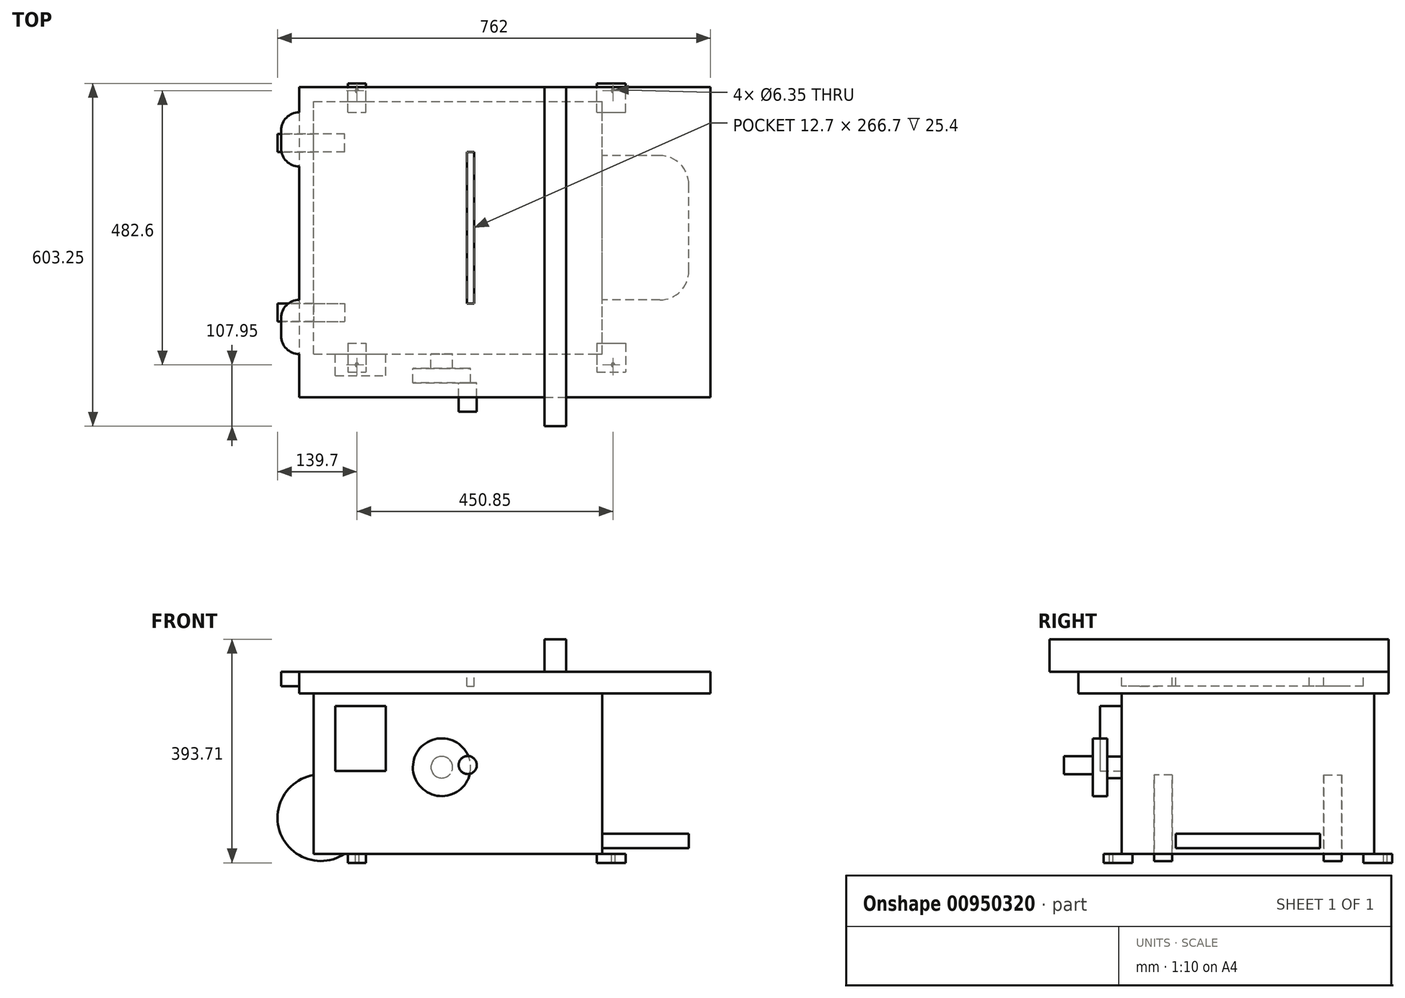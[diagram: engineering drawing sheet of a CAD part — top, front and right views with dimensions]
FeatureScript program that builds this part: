
annotation { "Feature Type Name" : "Feature", "Feature Type Description" : "" }
export const myFeature = defineFeature(function(context is Context, id is Id, definition is map)
    precondition{}
    {
        {
            var Q0;
            Q0=qCreatedBy(makeId("Top.planeOp"),FACE);
            var sketch = newSketch(context, id + "F0", { "sketchPlane" : qUnion([Q0])});
            skLineSegment(sketch, "E0.bottom", {"start": v(0, 0) * mm, "end": v(508, 0) * mm});
            skLineSegment(sketch, "E0.top", {"start": v(0, 444.5) * mm, "end": v(508, 444.5) * mm});
            skLineSegment(sketch, "E0.left", {"start": v(0, 0) * mm, "end": v(0, 444.5) * mm});
            skLineSegment(sketch, "E0.right", {"start": v(508, 0) * mm, "end": v(508, 444.5) * mm});
            skSolve(sketch);
        }
        {
            var Q0;
            Q0=qSketchRegion(id+"F0",true);
            extrude(context, id + "F1", {"entities" : qUnion([Q0]), "depth" : 282.57 * mm, "offsetDistance" : 25.4 * mm});
        }
        {
            var Q0;
            Q0=makeQuery(id+"F1.opExtrude","CAP_FACE",FACE,{"disambiguationData":[OSD([sQuery(id+"F0.wireOp",EDGE,"E0.bottom"),sQuery(id+"F0.wireOp",EDGE,"E0.top"),sQuery(id+"F0.wireOp",EDGE,"E0.left"),sQuery(id+"F0.wireOp",EDGE,"E0.right")])],"isStart":true});
            var sketch = newSketch(context, id + "F2", { "sketchPlane" : qUnion([Q0])});
            skLineSegment(sketch, "E1.bottom", {"start": v(60.32, -19.05) * mm, "end": v(92.07, -19.05) * mm});
            skLineSegment(sketch, "E1.top", {"start": v(60.32, 31.75) * mm, "end": v(92.07, 31.75) * mm});
            skLineSegment(sketch, "E1.left", {"start": v(60.32, -19.05) * mm, "end": v(60.32, 31.75) * mm});
            skLineSegment(sketch, "E1.right", {"start": v(92.07, -19.05) * mm, "end": v(92.07, 31.75) * mm});
            skLineSegment(sketch, "E2.bottom", {"start": v(498.48, -19.05) * mm, "end": v(549.28, -19.05) * mm});
            skLineSegment(sketch, "E2.top", {"start": v(498.48, 31.75) * mm, "end": v(549.28, 31.75) * mm});
            skLineSegment(sketch, "E2.left", {"start": v(498.48, -19.05) * mm, "end": v(498.48, 31.75) * mm});
            skLineSegment(sketch, "E2.right", {"start": v(549.28, -19.05) * mm, "end": v(549.28, 31.75) * mm});
            skLineSegment(sketch, "E3.bottom", {"start": v(60.33, -425.45) * mm, "end": v(92.08, -425.45) * mm});
            skLineSegment(sketch, "E3.top", {"start": v(60.33, -476.25) * mm, "end": v(92.08, -476.25) * mm});
            skLineSegment(sketch, "E3.left", {"start": v(60.33, -425.45) * mm, "end": v(60.33, -476.25) * mm});
            skLineSegment(sketch, "E3.right", {"start": v(92.08, -425.45) * mm, "end": v(92.08, -476.25) * mm});
            skLineSegment(sketch, "E4.bottom", {"start": v(498.48, -425.45) * mm, "end": v(549.28, -425.45) * mm});
            skLineSegment(sketch, "E4.top", {"start": v(498.48, -476.25) * mm, "end": v(549.28, -476.25) * mm});
            skLineSegment(sketch, "E4.left", {"start": v(498.48, -425.45) * mm, "end": v(498.48, -476.25) * mm});
            skLineSegment(sketch, "E4.right", {"start": v(549.28, -425.45) * mm, "end": v(549.28, -476.25) * mm});
            skLineSegment(sketch, "E5", {"start": v(76.2, -19.05) * mm, "end": v(76.2, 31.75) * mm, "construction": true});
            skLineSegment(sketch, "E6", {"start": v(76.2, -476.25) * mm, "end": v(76.2, -425.45) * mm, "construction": true});
            skLineSegment(sketch, "E7", {"start": v(523.88, -476.25) * mm, "end": v(523.88, -425.45) * mm, "construction": true});
            skSolve(sketch);
        }
        {
            var Q0;
            Q0=qSketchRegion(id+"F2",true);
            extrude(context, id + "F3", {"entities" : qUnion([Q0]), "operationType" : NewBodyOperationType.ADD, "depth" : 15.88 * mm, "offsetDistance" : 25.4 * mm});
        }
        {
            var Q0;
            Q0=makeQuery(id+"F1.opExtrude","CAP_FACE",FACE,{"disambiguationData":[OSD([sQuery(id+"F0.wireOp",EDGE,"E0.bottom"),sQuery(id+"F0.wireOp",EDGE,"E0.top"),sQuery(id+"F0.wireOp",EDGE,"E0.left"),sQuery(id+"F0.wireOp",EDGE,"E0.right")])],"isStart":false});
            var sketch = newSketch(context, id + "F4", { "sketchPlane" : qUnion([Q0])});
            skLineSegment(sketch, "E8.bottom", {"start": v(-25.4, 469.9) * mm, "end": v(698.5, 469.9) * mm});
            skLineSegment(sketch, "E8.top", {"start": v(-25.4, -76.2) * mm, "end": v(698.5, -76.2) * mm});
            skLineSegment(sketch, "E8.left", {"start": v(-25.4, 469.9) * mm, "end": v(-25.4, -76.2) * mm});
            skLineSegment(sketch, "E8.right", {"start": v(698.5, 469.9) * mm, "end": v(698.5, -76.2) * mm});
            skSolve(sketch);
        }
        {
            var Q0;
            Q0=qSketchRegion(id+"F4",true);
            extrude(context, id + "F5", {"entities" : qUnion([Q0]), "operationType" : NewBodyOperationType.ADD, "depth" : 38.1 * mm, "offsetDistance" : 25.4 * mm});
        }
        {
            var Q0;
            Q0=qCreatedBy(makeId("Front.planeOp"),FACE);
            var sketch = newSketch(context, id + "F6", { "sketchPlane" : qUnion([Q0])});
            skLineSegment(sketch, "E9", {"start": v(61.61, -15.88) * mm, "end": v(61.61, 320.68) * mm, "construction": true});
            skSolve(sketch);
        }
        {
            var Q0;
            Q0=makeQuery(id+"F5.opExtrude","CAP_FACE",FACE,{"disambiguationData":[OSD([sQuery(id+"F4.wireOp",EDGE,"E8.bottom"),sQuery(id+"F4.wireOp",EDGE,"E8.top"),sQuery(id+"F4.wireOp",EDGE,"E8.left"),sQuery(id+"F4.wireOp",EDGE,"E8.right")])],"isStart":false});
            var sketch = newSketch(context, id + "F7", { "sketchPlane" : qUnion([Q0])});
            skLineSegment(sketch, "E10.bottom", {"start": v(269.88, 355.6) * mm, "end": v(282.58, 355.6) * mm});
            skLineSegment(sketch, "E10.top", {"start": v(269.88, 88.9) * mm, "end": v(282.58, 88.9) * mm});
            skLineSegment(sketch, "E10.left", {"start": v(269.88, 355.6) * mm, "end": v(269.88, 88.9) * mm});
            skLineSegment(sketch, "E10.right", {"start": v(282.58, 355.6) * mm, "end": v(282.58, 88.9) * mm});
            skSolve(sketch);
        }
        {
            var Q0;
            Q0=qSketchRegion(id+"F7",true);
            extrude(context, id + "F8", {"entities" : qUnion([Q0]), "operationType" : NewBodyOperationType.REMOVE, "oppositeDirection" : true, "depth" : 25.4 * mm, "offsetDistance" : 25.4 * mm});
        }
        {
            var Q0;
            Q0=makeQuery(id+"F5.opExtrude","CAP_FACE",FACE,{"disambiguationData":[OSD([sQuery(id+"F4.wireOp",EDGE,"E8.bottom"),sQuery(id+"F4.wireOp",EDGE,"E8.top"),sQuery(id+"F4.wireOp",EDGE,"E8.left"),sQuery(id+"F4.wireOp",EDGE,"E8.right")])],"isStart":false});
            var sketch = newSketch(context, id + "F9", { "sketchPlane" : qUnion([Q0])});
            skLineSegment(sketch, "E11.bottom", {"start": v(406.7, 469.9) * mm, "end": v(444.8, 469.9) * mm});
            skLineSegment(sketch, "E11.top", {"start": v(406.7, -127) * mm, "end": v(444.8, -127) * mm});
            skLineSegment(sketch, "E11.left", {"start": v(406.7, 469.9) * mm, "end": v(406.7, -127) * mm});
            skLineSegment(sketch, "E11.right", {"start": v(444.8, 469.9) * mm, "end": v(444.8, -127) * mm});
            skSolve(sketch);
        }
        {
            var Q0;
            Q0=qSketchRegion(id+"F9",true);
            extrude(context, id + "F10", {"entities" : qUnion([Q0]), "operationType" : NewBodyOperationType.ADD, "depth" : 57.15 * mm, "offsetDistance" : 25.4 * mm});
        }
        {
            var Q0;
            Q0=makeQuery(id+"F1.opExtrude","SWEPT_FACE",FACE,{"disambiguationData":[OSD([sQuery(id+"F0.wireOp",EDGE,"E0.right")])]});
            var sketch = newSketch(context, id + "F11", { "sketchPlane" : qUnion([Q0])});
            skLineSegment(sketch, "E12.bottom", {"start": v(95.25, 10.16) * mm, "end": v(349.25, 10.16) * mm});
            skLineSegment(sketch, "E12.top", {"start": v(95.25, 35.56) * mm, "end": v(349.25, 35.56) * mm});
            skLineSegment(sketch, "E12.left", {"start": v(95.25, 10.16) * mm, "end": v(95.25, 35.56) * mm});
            skLineSegment(sketch, "E12.right", {"start": v(349.25, 10.16) * mm, "end": v(349.25, 35.56) * mm});
            skLineSegment(sketch, "E13", {"start": v(222.25, 10.16) * mm, "end": v(222.25, 35.56) * mm, "construction": true});
            skSolve(sketch);
        }
        {
            var Q0;
            Q0=qSketchRegion(id+"F11",true);
            extrude(context, id + "F12", {"entities" : qUnion([Q0]), "operationType" : NewBodyOperationType.ADD, "depth" : 152.4 * mm, "offsetDistance" : 25.4 * mm});
        }
        {
            var Q0;
            Q0=makeQuery(id+"F12.opExtrude","CAP_EDGE",EDGE,{"disambiguationData":[OSD([sQuery(id+"F11.wireOp",EDGE,"E12.left")])],"isStart":false});
            var Q1;
            Q1=makeQuery(id+"F12.opExtrude","CAP_EDGE",EDGE,{"disambiguationData":[OSD([sQuery(id+"F11.wireOp",EDGE,"E12.right")])],"isStart":false});
            fillet(context, id + "F13", {"entities" : qUnion([Q0, Q1]), "radius" : 50.8 * mm, "tangentPropagation" : true, "allowEdgeOverflow" : false});
        }
        {
            var Q0;
            {var subQ0=sQuery(id+"F4.wireOp",EDGE,"E8.left");var subQ3=sQuery(id+"F4.wireOp",EDGE,"E8.top");var subQ4=sQuery(id+"F4.wireOp",EDGE,"E8.bottom");Q0=makeQuery(id+"F10.boolean.opBoolean","SPLIT",FACE,{"disambiguationData":[TD([makeQuery(id+"F5.opExtrude","SWEPT_FACE",FACE,{"disambiguationData":[OSD([subQ0])]})])],"derivedFrom":makeQuery(id+"F5.opExtrude","CAP_FACE",FACE,{"disambiguationData":[OSD([subQ4,subQ3,subQ0,sQuery(id+"F4.wireOp",EDGE,"E8.right")])],"isStart":false})});}
            var sketch = newSketch(context, id + "F14", { "sketchPlane" : qUnion([Q0])});
            skLineSegment(sketch, "E14.bottom", {"start": v(-25.4, 0) * mm, "end": v(-25.4, 0) * mm});
            skLineSegment(sketch, "E14.top", {"start": v(-25.4, 95.25) * mm, "end": v(-25.4, 95.25) * mm});
            skLineSegment(sketch, "E14.left", {"start": v(-25.4, 0) * mm, "end": v(-25.4, 95.25) * mm});
            skLineSegment(sketch, "E14.right", {"start": v(-57.15, 31.75) * mm, "end": v(-57.15, 63.5) * mm});
            skLineSegment(sketch, "E15.bottom", {"start": v(-25.4, 425.45) * mm, "end": v(-25.4, 425.45) * mm});
            skLineSegment(sketch, "E15.top", {"start": v(-25.4, 330.2) * mm, "end": v(-25.4, 330.2) * mm});
            skLineSegment(sketch, "E15.left", {"start": v(-25.4, 425.45) * mm, "end": v(-25.4, 330.2) * mm});
            skLineSegment(sketch, "E15.right", {"start": v(-57.15, 393.7) * mm, "end": v(-57.15, 361.95) * mm});
            skPoint(sketch, "E16.visualSharp", {"position": v(-57.15, 95.25) * mm});
            skArc(sketch, "E16.filletArc", {"start": v(-25.4, 95.25) * mm, "mid": v(-47.85, 85.95) * mm, "end": v(-57.15, 63.5) * mm});
            skPoint(sketch, "E17.visualSharp", {"position": v(-57.15, 0) * mm});
            skArc(sketch, "E17.filletArc", {"start": v(-57.15, 31.75) * mm, "mid": v(-47.85, 9.3) * mm, "end": v(-25.4, 0) * mm});
            skPoint(sketch, "E18.visualSharp", {"position": v(-57.15, 425.45) * mm});
            skArc(sketch, "E18.filletArc", {"start": v(-25.4, 425.45) * mm, "mid": v(-47.85, 416.15) * mm, "end": v(-57.15, 393.7) * mm});
            skPoint(sketch, "E19.visualSharp", {"position": v(-57.15, 330.2) * mm});
            skArc(sketch, "E19.filletArc", {"start": v(-57.15, 361.95) * mm, "mid": v(-47.85, 339.5) * mm, "end": v(-25.4, 330.2) * mm});
            skSolve(sketch);
        }
        {
            var Q0;
            Q0=qSketchRegion(id+"F14",true);
            extrude(context, id + "F15", {"entities" : qUnion([Q0]), "operationType" : NewBodyOperationType.ADD, "oppositeDirection" : true, "depth" : 25.4 * mm, "offsetDistance" : 25.4 * mm});
        }
        {
            var Q0;
            Q0=makeQuery(id+"F1.opExtrude","SWEPT_FACE",FACE,{"disambiguationData":[OSD([sQuery(id+"F0.wireOp",EDGE,"E0.bottom")])]});
            cPlane(context, id + "F16", {"entities" : qUnion([Q0]), "cplaneType" : CPlaneType.OFFSET, "offset" : 57.15 * mm, "oppositeDirection" : true, "width" : 152.4 * mm, "height" : 152.4 * mm});
        }
        {
            var Q0;
            Q0=qCreatedBy(id+"F16.planeOp",FACE);
            var sketch = newSketch(context, id + "F17", { "sketchPlane" : qUnion([Q0])});
            skCircle(sketch, "E20", {"center": v(12.7, 63.5) * mm, "radius": 76.2 * mm});
            skSolve(sketch);
        }
        {
            var Q0;
            Q0=qSketchRegion(id+"F17",true);
            extrude(context, id + "F18", {"entities" : qUnion([Q0]), "operationType" : NewBodyOperationType.ADD, "oppositeDirection" : true, "depth" : 31.75 * mm, "offsetDistance" : 25.4 * mm});
        }
        {
            var Q0;
            Q0=makeQuery(id+"F1.opExtrude","SWEPT_FACE",FACE,{"disambiguationData":[OSD([sQuery(id+"F0.wireOp",EDGE,"E0.top")])]});
            cPlane(context, id + "F19", {"entities" : qUnion([Q0]), "cplaneType" : CPlaneType.OFFSET, "offset" : 57.15 * mm, "oppositeDirection" : true, "width" : 152.4 * mm, "height" : 152.4 * mm});
        }
        {
            var Q0;
            Q0=qCreatedBy(id+"F19.planeOp",FACE);
            var sketch = newSketch(context, id + "F20", { "sketchPlane" : qUnion([Q0])});
            skCircle(sketch, "E21", {"center": v(-12.7, 63.5) * mm, "radius": 76.2 * mm});
            skSolve(sketch);
        }
        {
            var Q0;
            Q0=qSketchRegion(id+"F20",true);
            extrude(context, id + "F21", {"entities" : qUnion([Q0]), "operationType" : NewBodyOperationType.ADD, "oppositeDirection" : true, "depth" : 31.75 * mm, "offsetDistance" : 25.4 * mm});
        }
        {
            var Q0;
            Q0=makeQuery(id+"F3.opExtrude","CAP_FACE",FACE,{"disambiguationData":[OSD([sQuery(id+"F2.wireOp",EDGE,"E1.bottom"),sQuery(id+"F2.wireOp",EDGE,"E1.top"),sQuery(id+"F2.wireOp",EDGE,"E1.left"),sQuery(id+"F2.wireOp",EDGE,"E1.right")])],"isStart":false});
            var sketch = newSketch(context, id + "F22", { "sketchPlane" : qUnion([Q0])});
            skCircle(sketch, "E22", {"center": v(76.2, 19.05) * mm, "radius": 3.18 * mm});
            skCircle(sketch, "E23", {"center": v(76.2, -463.55) * mm, "radius": 3.18 * mm});
            skCircle(sketch, "E24", {"center": v(527.05, -463.55) * mm, "radius": 3.18 * mm});
            skCircle(sketch, "E25", {"center": v(527.05, 19.05) * mm, "radius": 3.18 * mm});
            skSolve(sketch);
        }
        {
            var Q0;
            Q0=qSketchRegion(id+"F22",true);
            extrude(context, id + "F23", {"entities" : qUnion([Q0]), "operationType" : NewBodyOperationType.REMOVE, "oppositeDirection" : true, "depth" : 25.4 * mm, "offsetDistance" : 25.4 * mm});
        }
        {
            var Q0;
            Q0=makeQuery(id+"F1.opExtrude","SWEPT_FACE",FACE,{"disambiguationData":[OSD([sQuery(id+"F0.wireOp",EDGE,"E0.bottom")])]});
            var sketch = newSketch(context, id + "F24", { "sketchPlane" : qUnion([Q0])});
            skCircle(sketch, "E26", {"center": v(225.55, 152.4) * mm, "radius": 19.05 * mm});
            skSolve(sketch);
        }
        {
            var Q0;
            Q0=qSketchRegion(id+"F24",true);
            extrude(context, id + "F25", {"entities" : qUnion([Q0]), "operationType" : NewBodyOperationType.ADD, "depth" : 25.4 * mm, "offsetDistance" : 25.4 * mm});
        }
        {
            var Q0;
            Q0=makeQuery(id+"F25.opExtrude","CAP_FACE",FACE,{"disambiguationData":[OSD([sQuery(id+"F24.wireOp",EDGE,"E26")])],"isStart":false});
            var sketch = newSketch(context, id + "F26", { "sketchPlane" : qUnion([Q0])});
            skCircle(sketch, "E27", {"center": v(225.55, 152.4) * mm, "radius": 50.8 * mm});
            skSolve(sketch);
        }
        {
            var Q0;
            Q0=qSketchRegion(id+"F26",true);
            extrude(context, id + "F27", {"entities" : qUnion([Q0]), "operationType" : NewBodyOperationType.ADD, "depth" : 25.4 * mm, "offsetDistance" : 25.4 * mm});
        }
        {
            var Q0;
            Q0=makeQuery(id+"F27.opExtrude","CAP_FACE",FACE,{"disambiguationData":[OSD([sQuery(id+"F26.wireOp",EDGE,"E27")])],"isStart":false});
            var sketch = newSketch(context, id + "F28", { "sketchPlane" : qUnion([Q0])});
            skCircle(sketch, "E28", {"center": v(271.27, 156.26) * mm, "radius": 15.88 * mm});
            skSolve(sketch);
        }
        {
            var Q0;
            Q0=qSketchRegion(id+"F28",true);
            extrude(context, id + "F29", {"entities" : qUnion([Q0]), "operationType" : NewBodyOperationType.ADD, "depth" : 50.8 * mm, "offsetDistance" : 25.4 * mm});
        }
        {
            var Q0;
            Q0=makeQuery(id+"F1.opExtrude","SWEPT_FACE",FACE,{"disambiguationData":[OSD([sQuery(id+"F0.wireOp",EDGE,"E0.bottom")])]});
            var sketch = newSketch(context, id + "F30", { "sketchPlane" : qUnion([Q0])});
            skLineSegment(sketch, "E29.bottom", {"start": v(38.1, 260.35) * mm, "end": v(127, 260.35) * mm});
            skLineSegment(sketch, "E29.top", {"start": v(38.1, 146.05) * mm, "end": v(127, 146.05) * mm});
            skLineSegment(sketch, "E29.left", {"start": v(38.1, 260.35) * mm, "end": v(38.1, 146.05) * mm});
            skLineSegment(sketch, "E29.right", {"start": v(127, 260.35) * mm, "end": v(127, 146.05) * mm});
            skSolve(sketch);
        }
        {
            var Q0;
            Q0=qSketchRegion(id+"F30",true);
            extrude(context, id + "F31", {"entities" : qUnion([Q0]), "operationType" : NewBodyOperationType.ADD, "depth" : 38.1 * mm, "offsetDistance" : 25.4 * mm});
        }
    });
